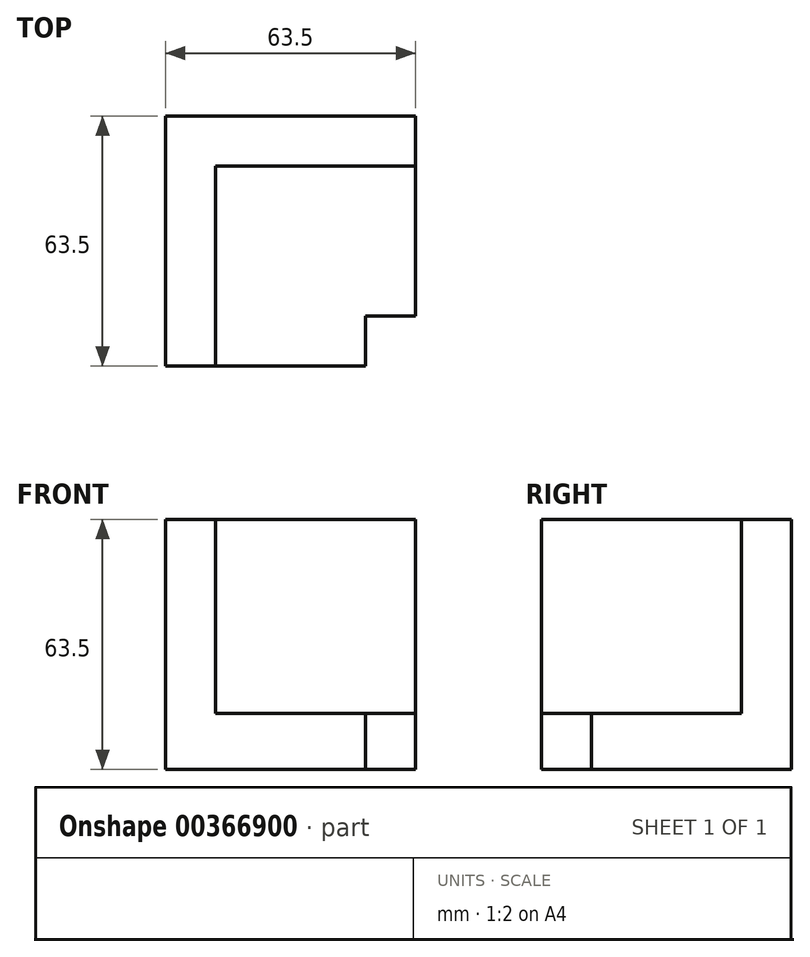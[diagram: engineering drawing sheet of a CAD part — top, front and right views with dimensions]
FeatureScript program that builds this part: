
annotation { "Feature Type Name" : "Feature", "Feature Type Description" : "" }
export const myFeature = defineFeature(function(context is Context, id is Id, definition is map)
    precondition{}
    {
        {
            var Q0;
            Q0=qCreatedBy(makeId("Front.planeOp"),FACE);
            var sketch = newSketch(context, id + "F0", { "sketchPlane" : qUnion([Q0])});
            skLineSegment(sketch, "E0.bottom", {"start": v(0, 0) * mm, "end": v(63.5, 0) * mm});
            skLineSegment(sketch, "E0.top", {"start": v(0, 63.5) * mm, "end": v(63.5, 63.5) * mm});
            skLineSegment(sketch, "E0.left", {"start": v(0, 0) * mm, "end": v(0, 63.5) * mm});
            skLineSegment(sketch, "E0.right", {"start": v(63.5, 0) * mm, "end": v(63.5, 63.5) * mm});
            skSolve(sketch);
        }
        {
            var Q0;
            Q0=makeQuery(id+"F0.imprint","IMPRINT",FACE,{"disambiguationData":[TD([[makeQuery(id+"F0.imprint","IMPRINT",EDGE,{"derivedFrom":sQuery(id+"F0.wireOp",EDGE,"E0.bottom")}),1.0]])]});
            extrude(context, id + "F1", {"entities" : qUnion([Q0]), "depth" : 63.5 * mm});
        }
        {
            var Q0;
            Q0=makeQuery(id+"F1.opExtrude","SWEPT_FACE",FACE,{"disambiguationData":[OSD([sQuery(id+"F0.wireOp",EDGE,"E0.top")])]});
            var sketch = newSketch(context, id + "F2", { "sketchPlane" : qUnion([Q0])});
            skLineSegment(sketch, "E1.bottom", {"start": v(63.5, -63.5) * mm, "end": v(12.7, -63.5) * mm});
            skLineSegment(sketch, "E1.top", {"start": v(63.5, -12.7) * mm, "end": v(12.7, -12.7) * mm});
            skLineSegment(sketch, "E1.left", {"start": v(63.5, -63.5) * mm, "end": v(63.5, -12.7) * mm});
            skLineSegment(sketch, "E1.right", {"start": v(12.7, -63.5) * mm, "end": v(12.7, -12.7) * mm});
            skSolve(sketch);
        }
        {
            var Q0;
            Q0=makeQuery(id+"F2.imprint","IMPRINT",FACE,{"disambiguationData":[TD([[makeQuery(id+"F2.imprint","IMPRINT",EDGE,{"derivedFrom":sQuery(id+"F2.wireOp",EDGE,"E1.bottom")}),1.0]])]});
            extrude(context, id + "F3", {"entities" : qUnion([Q0]), "operationType" : NewBodyOperationType.REMOVE, "oppositeDirection" : true, "depth" : 49.3 * mm});
        }
        {
            var Q0;
            Q0=makeQuery(id+"F3.boolean.opBoolean","COPY",FACE,{"derivedFrom":makeQuery(id+"F3.opExtrude","CAP_FACE",FACE,{"disambiguationData":[OSD([sQuery(id+"F2.wireOp",EDGE,"E1.bottom"),sQuery(id+"F2.wireOp",EDGE,"E1.top"),sQuery(id+"F2.wireOp",EDGE,"E1.left"),sQuery(id+"F2.wireOp",EDGE,"E1.right")])],"isStart":false})});
            var sketch = newSketch(context, id + "F4", { "sketchPlane" : qUnion([Q0])});
            skLineSegment(sketch, "E2.bottom", {"start": v(63.5, -63.5) * mm, "end": v(50.8, -63.5) * mm});
            skLineSegment(sketch, "E2.top", {"start": v(63.5, -50.8) * mm, "end": v(50.8, -50.8) * mm});
            skLineSegment(sketch, "E2.left", {"start": v(63.5, -63.5) * mm, "end": v(63.5, -50.8) * mm});
            skLineSegment(sketch, "E2.right", {"start": v(50.8, -63.5) * mm, "end": v(50.8, -50.8) * mm});
            skSolve(sketch);
        }
        {
            var Q0;
            Q0=makeQuery(id+"F4.imprint","IMPRINT",FACE,{"disambiguationData":[TD([[makeQuery(id+"F4.imprint","IMPRINT",EDGE,{"derivedFrom":sQuery(id+"F4.wireOp",EDGE,"E2.bottom")}),1.0]])]});
            var Q1;
            Q1 = qSketchRegion(id + "F4", true);
            extrude(context, id + "F5", {"entities" : qUnion([Q0, Q1]), "operationType" : NewBodyOperationType.REMOVE, "oppositeDirection" : true, "depth" : 25.4 * mm});
        }
    });
